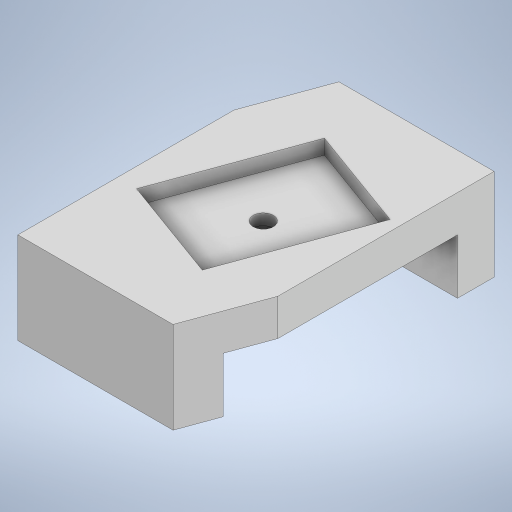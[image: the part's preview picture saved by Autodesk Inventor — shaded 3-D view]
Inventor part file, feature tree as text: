
AUTODESK INVENTOR PART (.ipt)
format: ipt  version: 2023.2 (Build 272271030, 271C)  size: 273,920 bytes
history: native  units: mm
features: extrude x5, sketch x5, projected_geometry x4, plane x3
ambient origin geometry x8: Origin, YZ Plane, XZ Plane, XY Plane, X Axis, Y Axis, Z Axis, Center Point
bodies: Solid1 (feature_tree)
feature tree (17):
  extrude  "Extrusion1"  Depth=80.0mm
  plane  "Work Plane1"
  extrude  "Extrusion2"  Depth=21.0mm
  plane  "Work Plane2"
  extrude  "Extrusion3"  Depth=21.0mm
  plane  "Work Plane3"
  extrude  "Extrusion4"  Depth=25.0mm
  extrude  "Extrusion5"  Depth=10.0mm
  sketch  "Sketch1"  dims[d0=50.0mm d1=80.0mm]
  sketch  "Sketch2"  dims[d2=21.0mm d3=3.490659mm]
  projected_geometry  "Projected Loop1"
  projected_geometry  "Projected Loop2"
  sketch  "Sketch3"  dims[d4=3.490659mm d5=21.0mm]
  projected_geometry  "Projected Loop3"
  sketch  "Sketch4"  dims[d6=25.0mm d7=0.0mm d8=25.25mm]
  projected_geometry  "Projected Loop4"
  sketch  "Sketch5"  dims[d9=60.0mm d10=10.0mm d11=15.0mm d12=0.0mm d13=0.0mm d14=25.0mm d15=30.0mm d16=40.0mm d17=30.0mm d18=25.0mm d19=12.217305mm d20=5.3mm d21=4.0mm d22=0.0mm d23=21.0mm d24=5.5mm d25=0.0mm d26=0.0mm d27=8.1mm d28=3.0mm d29=0.0mm]
